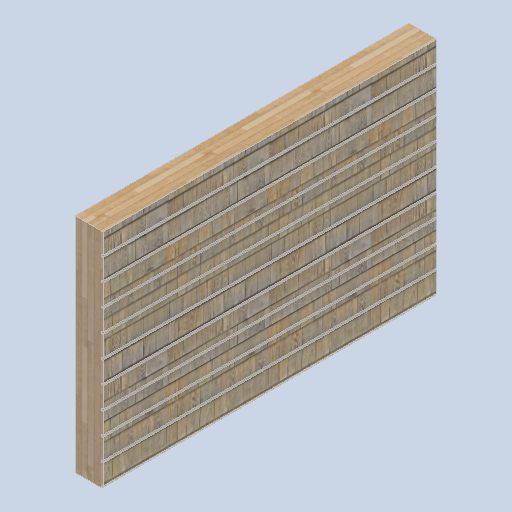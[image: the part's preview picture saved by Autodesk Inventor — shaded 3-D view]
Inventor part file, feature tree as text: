
AUTODESK INVENTOR PART (.ipt)
format: ipt  version: 2024.2 (Build 282272000, 272)  size: 372,224 bytes
history: native  units: in
note: dims shown in document units (in); Inventor stores cm internally (conversion verified against a paired STEP export)
features: other x3, sketch x1
ambient origin geometry x8: Origin, YZ Plane, XZ Plane, XY Plane, X Axis, Y Axis, Z Axis, Center Point
bodies: Solid1 (feature_tree)
feature tree (4):
  other  "side_wall_block_01_MIR.ipt"
  other  "Solid1::side_wall_block_01_MIR.ipt"
  other  "TaggingFeature1"
  sketch  "Sketch1"  dims[d0=0.3937in]
